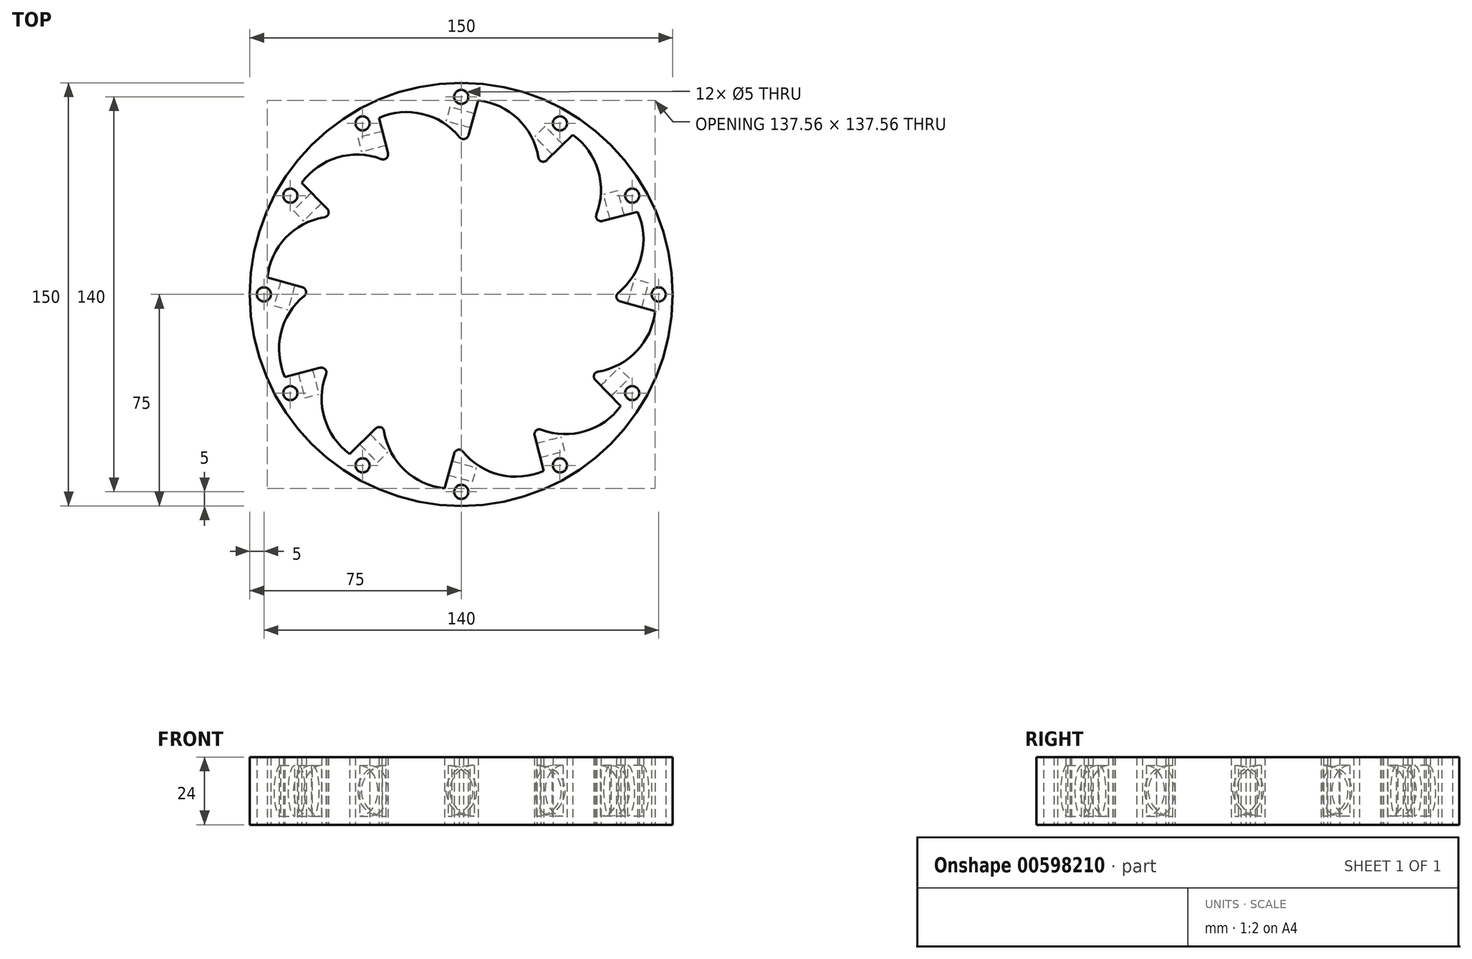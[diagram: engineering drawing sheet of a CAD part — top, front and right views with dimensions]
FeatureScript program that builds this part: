
annotation { "Feature Type Name" : "Feature", "Feature Type Description" : "" }
export const myFeature = defineFeature(function(context is Context, id is Id, definition is map)
    precondition{}
    {
        {
            var Q0;
            Q0=qCreatedBy(makeId("Top.planeOp"),FACE);
            var sketch = newSketch(context, id + "F0", { "sketchPlane" : qUnion([Q0])});
            skCircle(sketch, "E0", {"center": v(0, 0) * mm, "radius": 75 * mm});
            skLineSegment(sketch, "E1", {"start": v(0, 0) * mm, "end": v(-0.78, -1.35) * mm});
            skPoint(sketch, "E2.orphan", {"position": v(90.88, 52.47) * mm});
            skPoint(sketch, "E3.orphan", {"position": v(90.88, -52.47) * mm});
            skPoint(sketch, "E4.orphan", {"position": v(0, -93.78) * mm});
            skPoint(sketch, "E5.orphan", {"position": v(40.1, -69.46) * mm});
            skPoint(sketch, "E6.orphan", {"position": v(-44.19, -76.53) * mm});
            skPoint(sketch, "E7.orphan", {"position": v(-78.8, -46.4) * mm});
            skPoint(sketch, "E8.orphan", {"position": v(-78.8, 46.4) * mm});
            skPoint(sketch, "E9.orphan", {"position": v(-44.19, 76.53) * mm});
            skPoint(sketch, "E10.orphan", {"position": v(0, 93.78) * mm});
            skPoint(sketch, "E11.orphan", {"position": v(40.1, 69.46) * mm});
            skArc(sketch, "E12", {"start": v(48.67, 25.62) * mm, "mid": v(48.16, 26.57) * mm, "end": v(47.63, 27.5) * mm});
            skLineSegment(sketch, "E13", {"start": v(48.67, 25.62) * mm, "end": v(62.54, 29.24) * mm});
            skLineSegment(sketch, "E14", {"start": v(1.62, 0) * mm, "end": v(66.82, 0) * mm});
            skArc(sketch, "E15", {"start": v(55, 0) * mm, "mid": v(63.86, 13.3) * mm, "end": v(62.54, 29.24) * mm});
            skArc(sketch, "E16.1.0", {"start": v(47.63, 27.5) * mm, "mid": v(48.65, 43.46) * mm, "end": v(39.54, 56.6) * mm});
            skLineSegment(sketch, "E16.1.1", {"start": v(29.34, 46.52) * mm, "end": v(39.54, 56.6) * mm});
            skArc(sketch, "E16.2.0", {"start": v(27.5, 47.63) * mm, "mid": v(20.4, 61.96) * mm, "end": v(5.95, 68.78) * mm});
            skLineSegment(sketch, "E16.2.1", {"start": v(2.15, 54.96) * mm, "end": v(5.95, 68.78) * mm});
            skArc(sketch, "E16.3.0", {"start": v(0, 55) * mm, "mid": v(-13.3, 63.86) * mm, "end": v(-29.24, 62.54) * mm});
            skLineSegment(sketch, "E16.3.1", {"start": v(-25.62, 48.67) * mm, "end": v(-29.24, 62.54) * mm});
            skArc(sketch, "E16.4.0", {"start": v(-27.5, 47.63) * mm, "mid": v(-43.46, 48.65) * mm, "end": v(-56.6, 39.54) * mm});
            skLineSegment(sketch, "E16.4.1", {"start": v(-46.52, 29.34) * mm, "end": v(-56.6, 39.54) * mm});
            skArc(sketch, "E16.5.0", {"start": v(-47.63, 27.5) * mm, "mid": v(-61.96, 20.4) * mm, "end": v(-68.78, 5.95) * mm});
            skLineSegment(sketch, "E16.5.1", {"start": v(-54.96, 2.15) * mm, "end": v(-68.78, 5.95) * mm});
            skArc(sketch, "E16.6.0", {"start": v(-55, 0) * mm, "mid": v(-63.86, -13.3) * mm, "end": v(-62.54, -29.24) * mm});
            skLineSegment(sketch, "E16.6.1", {"start": v(-48.67, -25.62) * mm, "end": v(-62.54, -29.24) * mm});
            skArc(sketch, "E16.7.0", {"start": v(-47.63, -27.5) * mm, "mid": v(-48.65, -43.46) * mm, "end": v(-39.54, -56.6) * mm});
            skLineSegment(sketch, "E16.7.1", {"start": v(-29.34, -46.52) * mm, "end": v(-39.54, -56.6) * mm});
            skArc(sketch, "E16.8.0", {"start": v(-27.5, -47.63) * mm, "mid": v(-20.4, -61.96) * mm, "end": v(-5.95, -68.78) * mm});
            skLineSegment(sketch, "E16.8.1", {"start": v(-2.15, -54.96) * mm, "end": v(-5.95, -68.78) * mm});
            skArc(sketch, "E16.9.0", {"start": v(0, -55) * mm, "mid": v(13.3, -63.86) * mm, "end": v(29.24, -62.54) * mm});
            skLineSegment(sketch, "E16.9.1", {"start": v(25.62, -48.67) * mm, "end": v(29.24, -62.54) * mm});
            skArc(sketch, "E16.10.0", {"start": v(27.5, -47.63) * mm, "mid": v(43.46, -48.65) * mm, "end": v(56.6, -39.54) * mm});
            skLineSegment(sketch, "E16.10.1", {"start": v(46.52, -29.34) * mm, "end": v(56.6, -39.54) * mm});
            skArc(sketch, "E16.11.0", {"start": v(47.63, -27.5) * mm, "mid": v(61.96, -20.4) * mm, "end": v(68.78, -5.95) * mm});
            skLineSegment(sketch, "E16.11.1", {"start": v(54.96, -2.15) * mm, "end": v(68.78, -5.95) * mm});
            skArc(sketch, "E17.trimOffspring", {"start": v(54.96, -2.15) * mm, "mid": v(54.99, -1.07) * mm, "end": v(55, 0) * mm});
            skArc(sketch, "E18.trimOffspring", {"start": v(46.52, -29.34) * mm, "mid": v(47.09, -28.42) * mm, "end": v(47.63, -27.5) * mm});
            skArc(sketch, "E19.trimOffspring", {"start": v(25.62, -48.67) * mm, "mid": v(26.57, -48.16) * mm, "end": v(27.5, -47.63) * mm});
            skArc(sketch, "E20.trimOffspring", {"start": v(-2.15, -54.96) * mm, "mid": v(-1.07, -54.99) * mm, "end": v(0, -55) * mm});
            skArc(sketch, "E21.trimOffspring", {"start": v(-29.34, -46.52) * mm, "mid": v(-28.42, -47.09) * mm, "end": v(-27.5, -47.63) * mm});
            skArc(sketch, "E22.trimOffspring", {"start": v(-48.67, -25.62) * mm, "mid": v(-48.16, -26.57) * mm, "end": v(-47.63, -27.5) * mm});
            skArc(sketch, "E23.trimOffspring", {"start": v(-54.96, 2.15) * mm, "mid": v(-54.99, 1.07) * mm, "end": v(-55, 0) * mm});
            skArc(sketch, "E24.trimOffspring", {"start": v(-25.62, 48.67) * mm, "mid": v(-26.57, 48.16) * mm, "end": v(-27.5, 47.63) * mm});
            skArc(sketch, "E25.trimOffspring", {"start": v(2.15, 54.96) * mm, "mid": v(1.07, 54.99) * mm, "end": v(0, 55) * mm});
            skArc(sketch, "E26.trimOffspring", {"start": v(29.34, 46.52) * mm, "mid": v(28.42, 47.09) * mm, "end": v(27.5, 47.63) * mm});
            skCircle(sketch, "E27", {"center": v(0, 0) * mm, "radius": 55 * mm});
            skCircle(sketch, "E28", {"center": v(70, 0) * mm, "radius": 2.5 * mm});
            skCircle(sketch, "E29.1.0", {"center": v(60.62, 35) * mm, "radius": 2.5 * mm});
            skCircle(sketch, "E29.2.0", {"center": v(35, 60.62) * mm, "radius": 2.5 * mm});
            skCircle(sketch, "E29.3.0", {"center": v(0, 70) * mm, "radius": 2.5 * mm});
            skCircle(sketch, "E29.4.0", {"center": v(-35, 60.62) * mm, "radius": 2.5 * mm});
            skCircle(sketch, "E29.5.0", {"center": v(-60.62, 35) * mm, "radius": 2.5 * mm});
            skCircle(sketch, "E29.6.0", {"center": v(-70, 0) * mm, "radius": 2.5 * mm});
            skCircle(sketch, "E29.7.0", {"center": v(-60.62, -35) * mm, "radius": 2.5 * mm});
            skCircle(sketch, "E29.8.0", {"center": v(-35, -60.62) * mm, "radius": 2.5 * mm});
            skCircle(sketch, "E29.9.0", {"center": v(0, -70) * mm, "radius": 2.5 * mm});
            skCircle(sketch, "E29.10.0", {"center": v(35, -60.62) * mm, "radius": 2.5 * mm});
            skCircle(sketch, "E29.11.0", {"center": v(60.62, -35) * mm, "radius": 2.5 * mm});
            skSolve(sketch);
        }
        {
            var Q0;
            Q0=makeQuery(id+"F0.imprint","IMPRINT",FACE,{"disambiguationData":[TD([[makeQuery(id+"F0.imprint","IMPRINT",EDGE,{"derivedFrom":sQuery(id+"F0.wireOp",EDGE,"E0")}),1.0]])]});
            extrude(context, id + "F1", {"entities" : qUnion([Q0]), "depth" : 24 * mm, "offsetDistance" : 25 * mm});
        }
        {
            var Q0;
            Q0=makeQuery(id+"F1.opExtrude","SWEPT_EDGE",EDGE,{"disambiguationData":[OSD([sQuery(id+"F0.wireOp",EDGE,"E16.11.0"),sQuery(id+"F0.wireOp",EDGE,"E27")])]});
            var Q1;
            Q1=makeQuery(id+"F1.opExtrude","SWEPT_EDGE",EDGE,{"disambiguationData":[OSD([sQuery(id+"F0.wireOp",EDGE,"E16.10.1"),sQuery(id+"F0.wireOp",EDGE,"E27")])]});
            var Q2;
            Q2=makeQuery(id+"F1.opExtrude","SWEPT_EDGE",EDGE,{"disambiguationData":[OSD([sQuery(id+"F0.wireOp",EDGE,"E15"),sQuery(id+"F0.wireOp",EDGE,"E27")])]});
            var Q3;
            Q3=makeQuery(id+"F1.opExtrude","SWEPT_EDGE",EDGE,{"disambiguationData":[OSD([sQuery(id+"F0.wireOp",EDGE,"E16.11.1"),sQuery(id+"F0.wireOp",EDGE,"E27")])]});
            var Q4;
            Q4=makeQuery(id+"F1.opExtrude","SWEPT_EDGE",EDGE,{"disambiguationData":[OSD([sQuery(id+"F0.wireOp",EDGE,"E13"),sQuery(id+"F0.wireOp",EDGE,"E27")])]});
            var Q5;
            Q5=makeQuery(id+"F1.opExtrude","SWEPT_EDGE",EDGE,{"disambiguationData":[OSD([sQuery(id+"F0.wireOp",EDGE,"E16.1.0"),sQuery(id+"F0.wireOp",EDGE,"E27")])]});
            var Q6;
            Q6=makeQuery(id+"F1.opExtrude","SWEPT_EDGE",EDGE,{"disambiguationData":[OSD([sQuery(id+"F0.wireOp",EDGE,"E16.1.1"),sQuery(id+"F0.wireOp",EDGE,"E27")])]});
            var Q7;
            Q7=makeQuery(id+"F1.opExtrude","SWEPT_EDGE",EDGE,{"disambiguationData":[OSD([sQuery(id+"F0.wireOp",EDGE,"E16.2.0"),sQuery(id+"F0.wireOp",EDGE,"E27")])]});
            var Q8;
            Q8=makeQuery(id+"F1.opExtrude","SWEPT_EDGE",EDGE,{"disambiguationData":[OSD([sQuery(id+"F0.wireOp",EDGE,"E16.2.1"),sQuery(id+"F0.wireOp",EDGE,"E27")])]});
            var Q9;
            Q9=makeQuery(id+"F1.opExtrude","SWEPT_EDGE",EDGE,{"disambiguationData":[OSD([sQuery(id+"F0.wireOp",EDGE,"E16.3.0"),sQuery(id+"F0.wireOp",EDGE,"E27")])]});
            var Q10;
            Q10=makeQuery(id+"F1.opExtrude","SWEPT_EDGE",EDGE,{"disambiguationData":[OSD([sQuery(id+"F0.wireOp",EDGE,"E16.3.1"),sQuery(id+"F0.wireOp",EDGE,"E27")])]});
            var Q11;
            Q11=makeQuery(id+"F1.opExtrude","SWEPT_EDGE",EDGE,{"disambiguationData":[OSD([sQuery(id+"F0.wireOp",EDGE,"E16.4.0"),sQuery(id+"F0.wireOp",EDGE,"E27")])]});
            var Q12;
            Q12=makeQuery(id+"F1.opExtrude","SWEPT_EDGE",EDGE,{"disambiguationData":[OSD([sQuery(id+"F0.wireOp",EDGE,"E16.4.1"),sQuery(id+"F0.wireOp",EDGE,"E27")])]});
            var Q13;
            Q13=makeQuery(id+"F1.opExtrude","SWEPT_EDGE",EDGE,{"disambiguationData":[OSD([sQuery(id+"F0.wireOp",EDGE,"E16.5.0"),sQuery(id+"F0.wireOp",EDGE,"E27")])]});
            var Q14;
            Q14=makeQuery(id+"F1.opExtrude","SWEPT_EDGE",EDGE,{"disambiguationData":[OSD([sQuery(id+"F0.wireOp",EDGE,"E16.10.0"),sQuery(id+"F0.wireOp",EDGE,"E27")])]});
            var Q15;
            Q15=makeQuery(id+"F1.opExtrude","SWEPT_EDGE",EDGE,{"disambiguationData":[OSD([sQuery(id+"F0.wireOp",EDGE,"E16.9.1"),sQuery(id+"F0.wireOp",EDGE,"E27")])]});
            var Q16;
            Q16=makeQuery(id+"F1.opExtrude","SWEPT_EDGE",EDGE,{"disambiguationData":[OSD([sQuery(id+"F0.wireOp",EDGE,"E16.9.0"),sQuery(id+"F0.wireOp",EDGE,"E27")])]});
            var Q17;
            Q17=makeQuery(id+"F1.opExtrude","SWEPT_EDGE",EDGE,{"disambiguationData":[OSD([sQuery(id+"F0.wireOp",EDGE,"E16.8.1"),sQuery(id+"F0.wireOp",EDGE,"E27")])]});
            var Q18;
            Q18=makeQuery(id+"F1.opExtrude","SWEPT_EDGE",EDGE,{"disambiguationData":[OSD([sQuery(id+"F0.wireOp",EDGE,"E16.8.0"),sQuery(id+"F0.wireOp",EDGE,"E27")])]});
            var Q19;
            Q19=makeQuery(id+"F1.opExtrude","SWEPT_EDGE",EDGE,{"disambiguationData":[OSD([sQuery(id+"F0.wireOp",EDGE,"E16.7.1"),sQuery(id+"F0.wireOp",EDGE,"E27")])]});
            var Q20;
            Q20=makeQuery(id+"F1.opExtrude","SWEPT_EDGE",EDGE,{"disambiguationData":[OSD([sQuery(id+"F0.wireOp",EDGE,"E16.7.0"),sQuery(id+"F0.wireOp",EDGE,"E27")])]});
            var Q21;
            Q21=makeQuery(id+"F1.opExtrude","SWEPT_EDGE",EDGE,{"disambiguationData":[OSD([sQuery(id+"F0.wireOp",EDGE,"E16.6.1"),sQuery(id+"F0.wireOp",EDGE,"E27")])]});
            var Q22;
            Q22=makeQuery(id+"F1.opExtrude","SWEPT_EDGE",EDGE,{"disambiguationData":[OSD([sQuery(id+"F0.wireOp",EDGE,"E16.6.0"),sQuery(id+"F0.wireOp",EDGE,"E27")])]});
            var Q23;
            Q23=makeQuery(id+"F1.opExtrude","SWEPT_EDGE",EDGE,{"disambiguationData":[OSD([sQuery(id+"F0.wireOp",EDGE,"E16.5.1"),sQuery(id+"F0.wireOp",EDGE,"E27")])]});
            fillet(context, id + "F2", {"entities" : qUnion([Q0, Q1, Q2, Q3, Q4, Q5, Q6, Q7, Q8, Q9, Q10, Q11, Q12, Q13, Q14, Q15, Q16, Q17, Q18, Q19, Q20, Q21, Q22, Q23]), "radius" : 2 * mm, "tangentPropagation" : true, "allowEdgeOverflow" : false});
        }
        {
            var Q0;
            Q0=makeQuery(id+"F1.opExtrude","SWEPT_FACE",FACE,{"disambiguationData":[OSD([sQuery(id+"F0.wireOp",EDGE,"E13")])]});
            var sketch = newSketch(context, id + "F3", { "sketchPlane" : qUnion([Q0])});
            skLineSegment(sketch, "E30", {"start": v(63, 12) * mm, "end": v(57.8, 12) * mm});
            skLineSegment(sketch, "E31", {"start": v(57.8, 12) * mm, "end": v(57.8, 21) * mm});
            skLineSegment(sketch, "E32", {"start": v(57.8, 21) * mm, "end": v(63, 21) * mm});
            skLineSegment(sketch, "E33", {"start": v(63, 21) * mm, "end": v(63, 12) * mm});
            skPoint(sketch, "E34.orphan", {"position": v(67.9, 12) * mm});
            skSolve(sketch);
        }
        {
            var Q0;
            Q0=makeQuery(id+"F3.imprint","IMPRINT",FACE,{"disambiguationData":[TD([[makeQuery(id+"F3.imprint","IMPRINT",EDGE,{"derivedFrom":sQuery(id+"F3.wireOp",EDGE,"E30")}),-1.0]])]});
            var Q1;
            Q1=sQuery(id+"F3.wireOp",EDGE,"E30");
            revolve(context, id + "F4", {"operationType" : NewBodyOperationType.REMOVE, "entities" : qUnion([Q0]), "axis" : qUnion([Q1]), "revolveType" : RevolveType.FULL, "oppositeDirection" : true});
        }
        {
            var Q0;
            Q0=makeQuery(id+"F1.opExtrude","SWEPT_FACE",FACE,{"disambiguationData":[OSD([sQuery(id+"F0.wireOp",EDGE,"E16.11.1")])]});
            var sketch = newSketch(context, id + "F5", { "sketchPlane" : qUnion([Q0])});
            skLineSegment(sketch, "E35", {"start": v(63, 12) * mm, "end": v(57.8, 12) * mm});
            skPoint(sketch, "E35.endSnap0", {"position": v(67.9, 12) * mm});
            skLineSegment(sketch, "E36", {"start": v(57.8, 12) * mm, "end": v(57.8, 21) * mm});
            skLineSegment(sketch, "E37", {"start": v(57.8, 21) * mm, "end": v(63, 21) * mm});
            skLineSegment(sketch, "E38", {"start": v(63, 21) * mm, "end": v(63, 12) * mm});
            skSolve(sketch);
        }
        {
            var Q0;
            Q0=makeQuery(id+"F5.imprint","IMPRINT",FACE,{"disambiguationData":[TD([[makeQuery(id+"F5.imprint","IMPRINT",EDGE,{"derivedFrom":sQuery(id+"F5.wireOp",EDGE,"E35")}),-1.0]])]});
            var Q1;
            Q1=sQuery(id+"F5.wireOp",EDGE,"E35");
            revolve(context, id + "F6", {"operationType" : NewBodyOperationType.REMOVE, "entities" : qUnion([Q0]), "axis" : qUnion([Q1]), "revolveType" : RevolveType.FULL, "oppositeDirection" : true});
        }
        {
            var Q0;
            Q0=makeQuery(id+"F1.opExtrude","SWEPT_FACE",FACE,{"disambiguationData":[OSD([sQuery(id+"F0.wireOp",EDGE,"E16.10.1")])]});
            var sketch = newSketch(context, id + "F7", { "sketchPlane" : qUnion([Q0])});
            skLineSegment(sketch, "E39", {"start": v(63, 12) * mm, "end": v(57.8, 12) * mm});
            skPoint(sketch, "E39.endSnap0", {"position": v(67.9, 12) * mm});
            skLineSegment(sketch, "E40", {"start": v(57.8, 12) * mm, "end": v(57.8, 21) * mm});
            skLineSegment(sketch, "E41", {"start": v(57.8, 21) * mm, "end": v(63, 21) * mm});
            skLineSegment(sketch, "E42", {"start": v(63, 21) * mm, "end": v(63, 12) * mm});
            skSolve(sketch);
        }
        {
            var Q0;
            Q0=makeQuery(id+"F7.imprint","IMPRINT",FACE,{"disambiguationData":[TD([[makeQuery(id+"F7.imprint","IMPRINT",EDGE,{"derivedFrom":sQuery(id+"F7.wireOp",EDGE,"E39")}),-1.0]])]});
            var Q1;
            Q1=sQuery(id+"F7.wireOp",EDGE,"E39");
            revolve(context, id + "F8", {"operationType" : NewBodyOperationType.REMOVE, "entities" : qUnion([Q0]), "axis" : qUnion([Q1]), "revolveType" : RevolveType.FULL, "oppositeDirection" : true});
        }
        {
            var Q0;
            Q0=makeQuery(id+"F1.opExtrude","SWEPT_FACE",FACE,{"disambiguationData":[OSD([sQuery(id+"F0.wireOp",EDGE,"E16.9.1")])]});
            var sketch = newSketch(context, id + "F9", { "sketchPlane" : qUnion([Q0])});
            skLineSegment(sketch, "E43", {"start": v(63, 12) * mm, "end": v(57.8, 12) * mm});
            skLineSegment(sketch, "E44", {"start": v(57.8, 12) * mm, "end": v(57.8, 21) * mm});
            skLineSegment(sketch, "E45", {"start": v(57.8, 21) * mm, "end": v(63, 21) * mm});
            skLineSegment(sketch, "E46", {"start": v(63, 21) * mm, "end": v(63, 12) * mm});
            skPoint(sketch, "E47.orphan", {"position": v(67.9, 12) * mm});
            skSolve(sketch);
        }
        {
            var Q0;
            Q0=makeQuery(id+"F9.imprint","IMPRINT",FACE,{"disambiguationData":[TD([[makeQuery(id+"F9.imprint","IMPRINT",EDGE,{"derivedFrom":sQuery(id+"F9.wireOp",EDGE,"E43")}),-1.0]])]});
            var Q1;
            Q1=sQuery(id+"F9.wireOp",EDGE,"E43");
            revolve(context, id + "F10", {"operationType" : NewBodyOperationType.REMOVE, "entities" : qUnion([Q0]), "axis" : qUnion([Q1]), "revolveType" : RevolveType.FULL, "oppositeDirection" : true});
        }
        {
            var Q0;
            Q0=makeQuery(id+"F1.opExtrude","SWEPT_FACE",FACE,{"disambiguationData":[OSD([sQuery(id+"F0.wireOp",EDGE,"E16.8.1")])]});
            var sketch = newSketch(context, id + "F11", { "sketchPlane" : qUnion([Q0])});
            skLineSegment(sketch, "E48", {"start": v(63, 12) * mm, "end": v(57.8, 12) * mm});
            skLineSegment(sketch, "E49", {"start": v(57.8, 12) * mm, "end": v(57.8, 21) * mm});
            skLineSegment(sketch, "E50", {"start": v(57.8, 21) * mm, "end": v(63, 21) * mm});
            skLineSegment(sketch, "E51", {"start": v(63, 21) * mm, "end": v(63, 12) * mm});
            skPoint(sketch, "E52.orphan", {"position": v(67.9, 12) * mm});
            skSolve(sketch);
        }
        {
            var Q0;
            Q0=makeQuery(id+"F11.imprint","IMPRINT",FACE,{"disambiguationData":[TD([[makeQuery(id+"F11.imprint","IMPRINT",EDGE,{"derivedFrom":sQuery(id+"F11.wireOp",EDGE,"E48")}),-1.0]])]});
            var Q1;
            Q1=sQuery(id+"F11.wireOp",EDGE,"E48");
            revolve(context, id + "F12", {"operationType" : NewBodyOperationType.REMOVE, "entities" : qUnion([Q0]), "axis" : qUnion([Q1]), "revolveType" : RevolveType.FULL, "oppositeDirection" : true});
        }
        {
            var Q0;
            Q0=makeQuery(id+"F1.opExtrude","SWEPT_FACE",FACE,{"disambiguationData":[OSD([sQuery(id+"F0.wireOp",EDGE,"E16.7.1")])]});
            var sketch = newSketch(context, id + "F13", { "sketchPlane" : qUnion([Q0])});
            skLineSegment(sketch, "E53", {"start": v(63, 12) * mm, "end": v(57.8, 12) * mm});
            skLineSegment(sketch, "E54", {"start": v(57.8, 12) * mm, "end": v(57.8, 21) * mm});
            skLineSegment(sketch, "E55", {"start": v(57.8, 21) * mm, "end": v(63, 21) * mm});
            skLineSegment(sketch, "E56", {"start": v(63, 21) * mm, "end": v(63, 12) * mm});
            skPoint(sketch, "E57.orphan", {"position": v(67.9, 12) * mm});
            skSolve(sketch);
        }
        {
            var Q0;
            Q0=makeQuery(id+"F13.imprint","IMPRINT",FACE,{"disambiguationData":[TD([[makeQuery(id+"F13.imprint","IMPRINT",EDGE,{"derivedFrom":sQuery(id+"F13.wireOp",EDGE,"E53")}),-1.0]])]});
            var Q1;
            Q1=sQuery(id+"F13.wireOp",EDGE,"E53");
            revolve(context, id + "F14", {"operationType" : NewBodyOperationType.REMOVE, "entities" : qUnion([Q0]), "axis" : qUnion([Q1]), "revolveType" : RevolveType.FULL, "oppositeDirection" : true});
        }
        {
            var Q0;
            Q0=makeQuery(id+"F1.opExtrude","SWEPT_FACE",FACE,{"disambiguationData":[OSD([sQuery(id+"F0.wireOp",EDGE,"E16.6.1")])]});
            var sketch = newSketch(context, id + "F15", { "sketchPlane" : qUnion([Q0])});
            skLineSegment(sketch, "E58", {"start": v(63, 12) * mm, "end": v(57.8, 12) * mm});
            skPoint(sketch, "E58.endSnap0", {"position": v(67.9, 12) * mm});
            skLineSegment(sketch, "E59", {"start": v(57.8, 12) * mm, "end": v(57.8, 21) * mm});
            skLineSegment(sketch, "E60", {"start": v(57.8, 21) * mm, "end": v(63, 21) * mm});
            skLineSegment(sketch, "E61", {"start": v(63, 21) * mm, "end": v(63, 12) * mm});
            skSolve(sketch);
        }
        {
            var Q0;
            Q0=makeQuery(id+"F15.imprint","IMPRINT",FACE,{"disambiguationData":[TD([[makeQuery(id+"F15.imprint","IMPRINT",EDGE,{"derivedFrom":sQuery(id+"F15.wireOp",EDGE,"E58")}),-1.0]])]});
            var Q1;
            Q1=sQuery(id+"F15.wireOp",EDGE,"E58");
            revolve(context, id + "F16", {"operationType" : NewBodyOperationType.REMOVE, "entities" : qUnion([Q0]), "axis" : qUnion([Q1]), "revolveType" : RevolveType.FULL, "oppositeDirection" : true});
        }
        {
            var Q0;
            Q0=makeQuery(id+"F1.opExtrude","SWEPT_FACE",FACE,{"disambiguationData":[OSD([sQuery(id+"F0.wireOp",EDGE,"E16.5.1")])]});
            var sketch = newSketch(context, id + "F17", { "sketchPlane" : qUnion([Q0])});
            skLineSegment(sketch, "E62", {"start": v(63, 12) * mm, "end": v(57.8, 12) * mm});
            skLineSegment(sketch, "E63", {"start": v(57.8, 12) * mm, "end": v(57.8, 21) * mm});
            skLineSegment(sketch, "E64", {"start": v(57.8, 21) * mm, "end": v(63, 21) * mm});
            skLineSegment(sketch, "E65", {"start": v(63, 21) * mm, "end": v(63, 12) * mm});
            skPoint(sketch, "E66.orphan", {"position": v(67.9, 12) * mm});
            skSolve(sketch);
        }
        {
            var Q0;
            Q0=makeQuery(id+"F17.imprint","IMPRINT",FACE,{"disambiguationData":[TD([[makeQuery(id+"F17.imprint","IMPRINT",EDGE,{"derivedFrom":sQuery(id+"F17.wireOp",EDGE,"E62")}),-1.0]])]});
            var Q1;
            Q1=sQuery(id+"F17.wireOp",EDGE,"E62");
            revolve(context, id + "F18", {"operationType" : NewBodyOperationType.REMOVE, "entities" : qUnion([Q0]), "axis" : qUnion([Q1]), "revolveType" : RevolveType.FULL, "oppositeDirection" : true});
        }
        {
            var Q0;
            Q0=makeQuery(id+"F1.opExtrude","SWEPT_FACE",FACE,{"disambiguationData":[OSD([sQuery(id+"F0.wireOp",EDGE,"E16.4.1")])]});
            var sketch = newSketch(context, id + "F19", { "sketchPlane" : qUnion([Q0])});
            skLineSegment(sketch, "E67", {"start": v(63, 12) * mm, "end": v(57.8, 12) * mm});
            skPoint(sketch, "E67.endSnap0", {"position": v(67.9, 12) * mm});
            skLineSegment(sketch, "E68", {"start": v(57.8, 12) * mm, "end": v(57.8, 21) * mm});
            skLineSegment(sketch, "E69", {"start": v(57.8, 21) * mm, "end": v(63, 21) * mm});
            skLineSegment(sketch, "E70", {"start": v(63, 21) * mm, "end": v(63, 12) * mm});
            skSolve(sketch);
        }
        {
            var Q0;
            Q0=makeQuery(id+"F19.imprint","IMPRINT",FACE,{"disambiguationData":[TD([[makeQuery(id+"F19.imprint","IMPRINT",EDGE,{"derivedFrom":sQuery(id+"F19.wireOp",EDGE,"E67")}),-1.0]])]});
            var Q1;
            Q1=sQuery(id+"F19.wireOp",EDGE,"E67");
            revolve(context, id + "F20", {"operationType" : NewBodyOperationType.REMOVE, "entities" : qUnion([Q0]), "axis" : qUnion([Q1]), "revolveType" : RevolveType.FULL, "oppositeDirection" : true});
        }
        {
            var Q0;
            Q0=makeQuery(id+"F1.opExtrude","SWEPT_FACE",FACE,{"disambiguationData":[OSD([sQuery(id+"F0.wireOp",EDGE,"E16.3.1")])]});
            var sketch = newSketch(context, id + "F21", { "sketchPlane" : qUnion([Q0])});
            skLineSegment(sketch, "E71", {"start": v(63, 12) * mm, "end": v(57.8, 12) * mm});
            skLineSegment(sketch, "E72", {"start": v(57.8, 12) * mm, "end": v(57.8, 21) * mm});
            skLineSegment(sketch, "E73", {"start": v(57.8, 21) * mm, "end": v(63, 21) * mm});
            skLineSegment(sketch, "E74", {"start": v(63, 21) * mm, "end": v(63, 12) * mm});
            skPoint(sketch, "E75.orphan", {"position": v(67.9, 12) * mm});
            skSolve(sketch);
        }
        {
            var Q0;
            Q0=makeQuery(id+"F21.imprint","IMPRINT",FACE,{"disambiguationData":[TD([[makeQuery(id+"F21.imprint","IMPRINT",EDGE,{"derivedFrom":sQuery(id+"F21.wireOp",EDGE,"E71")}),-1.0]])]});
            var Q1;
            Q1=sQuery(id+"F21.wireOp",EDGE,"E71");
            revolve(context, id + "F22", {"operationType" : NewBodyOperationType.REMOVE, "entities" : qUnion([Q0]), "axis" : qUnion([Q1]), "revolveType" : RevolveType.FULL, "oppositeDirection" : true});
        }
        {
            var Q0;
            Q0=makeQuery(id+"F1.opExtrude","SWEPT_FACE",FACE,{"disambiguationData":[OSD([sQuery(id+"F0.wireOp",EDGE,"E16.2.1")])]});
            var sketch = newSketch(context, id + "F23", { "sketchPlane" : qUnion([Q0])});
            skLineSegment(sketch, "E76", {"start": v(63, 12) * mm, "end": v(57.8, 12) * mm});
            skPoint(sketch, "E76.endSnap0", {"position": v(67.9, 12) * mm});
            skLineSegment(sketch, "E77", {"start": v(57.8, 12) * mm, "end": v(57.8, 21) * mm});
            skLineSegment(sketch, "E78", {"start": v(57.8, 21) * mm, "end": v(63, 21) * mm});
            skLineSegment(sketch, "E79", {"start": v(63, 21) * mm, "end": v(63, 12) * mm});
            skSolve(sketch);
        }
        {
            var Q0;
            Q0=makeQuery(id+"F23.imprint","IMPRINT",FACE,{"disambiguationData":[TD([[makeQuery(id+"F23.imprint","IMPRINT",EDGE,{"derivedFrom":sQuery(id+"F23.wireOp",EDGE,"E76")}),-1.0]])]});
            var Q1;
            Q1=sQuery(id+"F23.wireOp",EDGE,"E76");
            revolve(context, id + "F24", {"operationType" : NewBodyOperationType.REMOVE, "entities" : qUnion([Q0]), "axis" : qUnion([Q1]), "revolveType" : RevolveType.FULL, "oppositeDirection" : true});
        }
        {
            var Q0;
            Q0=makeQuery(id+"F1.opExtrude","SWEPT_FACE",FACE,{"disambiguationData":[OSD([sQuery(id+"F0.wireOp",EDGE,"E16.1.1")])]});
            var sketch = newSketch(context, id + "F25", { "sketchPlane" : qUnion([Q0])});
            skLineSegment(sketch, "E80", {"start": v(63, 12) * mm, "end": v(57.8, 12) * mm});
            skLineSegment(sketch, "E81", {"start": v(57.8, 12) * mm, "end": v(57.8, 21) * mm});
            skLineSegment(sketch, "E82", {"start": v(57.8, 21) * mm, "end": v(63, 21) * mm});
            skLineSegment(sketch, "E83", {"start": v(63, 21) * mm, "end": v(63, 12) * mm});
            skPoint(sketch, "E84.orphan", {"position": v(67.9, 12) * mm});
            skSolve(sketch);
        }
        {
            var Q0;
            Q0=makeQuery(id+"F25.imprint","IMPRINT",FACE,{"disambiguationData":[TD([[makeQuery(id+"F25.imprint","IMPRINT",EDGE,{"derivedFrom":sQuery(id+"F25.wireOp",EDGE,"E80")}),-1.0]])]});
            var Q1;
            Q1=sQuery(id+"F25.wireOp",EDGE,"E80");
            revolve(context, id + "F26", {"operationType" : NewBodyOperationType.REMOVE, "entities" : qUnion([Q0]), "axis" : qUnion([Q1]), "revolveType" : RevolveType.FULL, "oppositeDirection" : true});
        }
    });
